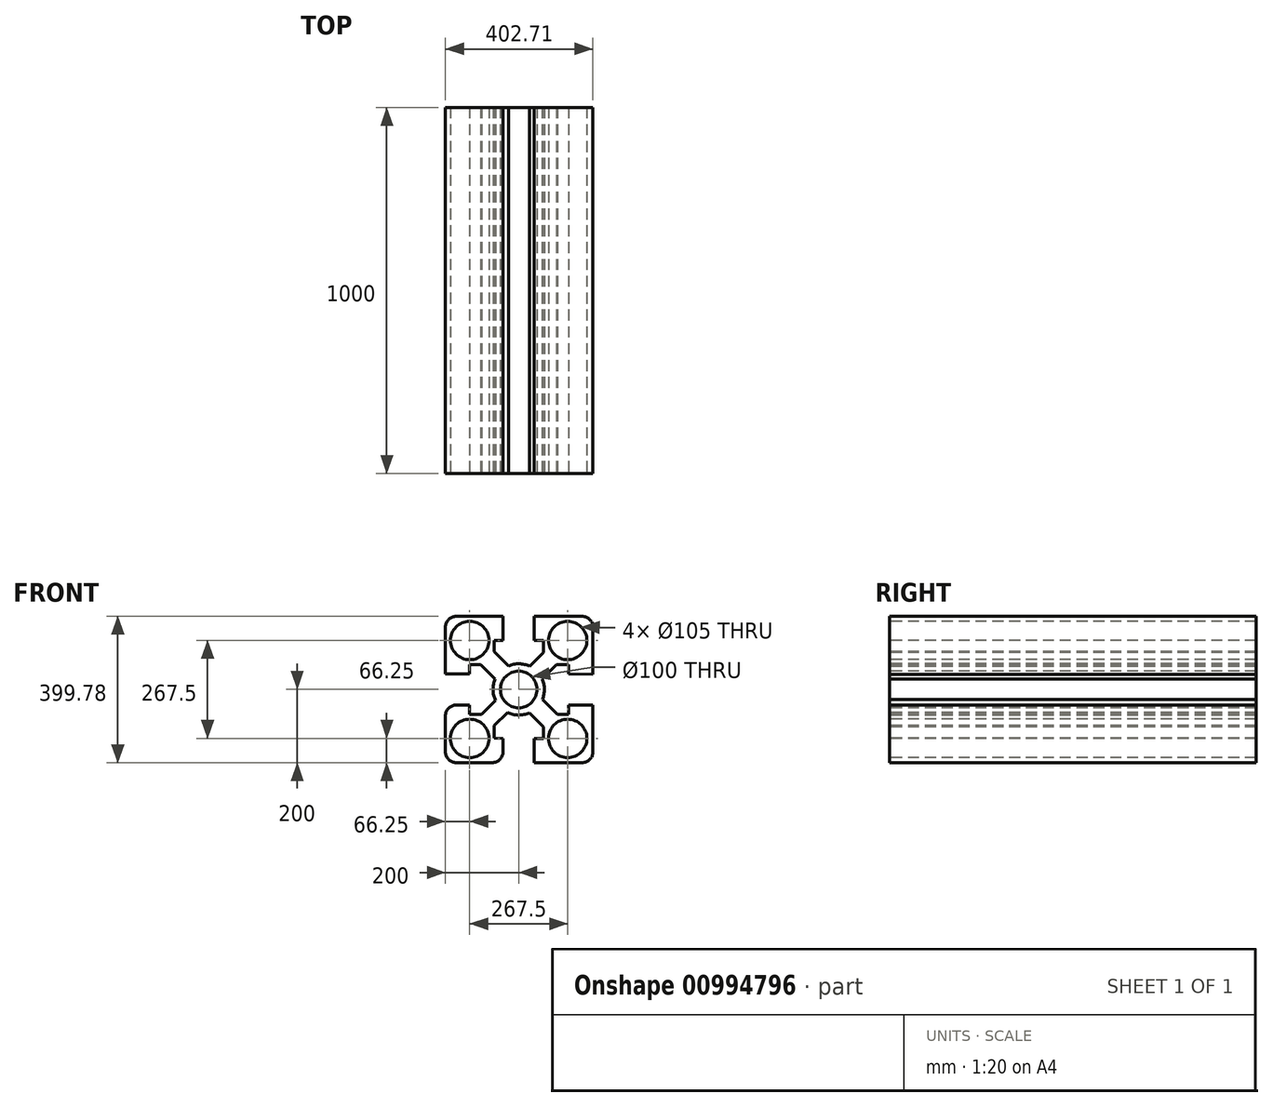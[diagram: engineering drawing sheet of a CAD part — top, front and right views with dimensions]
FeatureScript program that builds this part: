
annotation { "Feature Type Name" : "Feature", "Feature Type Description" : "" }
export const myFeature = defineFeature(function(context is Context, id is Id, definition is map)
    precondition{}
    {
        {
            var Q0;
            Q0=qCreatedBy(makeId("Front.planeOp"),FACE);
            var sketch = newSketch(context, id + "F0", { "sketchPlane" : qUnion([Q0])});
            skLineSegment(sketch, "E0", {"start": v(-200, -200) * mm, "end": v(-200, -133.75) * mm});
            skLineSegment(sketch, "E1", {"start": v(202.71, 199.78) * mm, "end": v(42.5, 199.78) * mm});
            skLineSegment(sketch, "E2", {"start": v(42.5, 199.78) * mm, "end": v(42.5, 133.75) * mm});
            skLineSegment(sketch, "E3", {"start": v(42.5, 133.75) * mm, "end": v(67.5, 133.75) * mm});
            skLineSegment(sketch, "E4", {"start": v(67.5, 133.75) * mm, "end": v(67.5, 100.95) * mm});
            skLineSegment(sketch, "E5", {"start": v(-100.85, -67.6) * mm, "end": v(-133.75, -67.6) * mm});
            skLineSegment(sketch, "E6", {"start": v(-133.75, -67.6) * mm, "end": v(-133.75, -42.5) * mm});
            skLineSegment(sketch, "E7", {"start": v(-133.75, -42.5) * mm, "end": v(-200, -42.5) * mm});
            skLineSegment(sketch, "E8", {"start": v(-200, -42.5) * mm, "end": v(-200, -200) * mm});
            skLineSegment(sketch, "E9", {"start": v(-42.5, -200) * mm, "end": v(-42.5, -133.75) * mm});
            skLineSegment(sketch, "E10", {"start": v(-42.5, -133.75) * mm, "end": v(-67.5, -133.3) * mm});
            skLineSegment(sketch, "E11", {"start": v(-67.5, -133.3) * mm, "end": v(-67.5, -98.5) * mm});
            skLineSegment(sketch, "E12", {"start": v(103.73, 67.4) * mm, "end": v(136.46, 67.4) * mm});
            skLineSegment(sketch, "E13", {"start": v(136.46, 67.4) * mm, "end": v(136.46, 42.5) * mm});
            skLineSegment(sketch, "E14", {"start": v(136.46, 42.5) * mm, "end": v(202.71, 41.3) * mm});
            skLineSegment(sketch, "E15", {"start": v(202.71, 41.3) * mm, "end": v(202.71, 199.78) * mm});
            skLineSegment(sketch, "E16", {"start": v(-42.5, 133.75) * mm, "end": v(-67.5, 133.75) * mm});
            skLineSegment(sketch, "E17", {"start": v(-67.5, 133.75) * mm, "end": v(-67.5, 103.43) * mm});
            skLineSegment(sketch, "E18", {"start": v(105.64, -67.6) * mm, "end": v(136.46, -67.6) * mm});
            skLineSegment(sketch, "E19", {"start": v(136.46, -67.6) * mm, "end": v(136.46, -42.5) * mm});
            skLineSegment(sketch, "E20", {"start": v(136.46, -42.5) * mm, "end": v(202.71, -42.5) * mm});
            skLineSegment(sketch, "E21", {"start": v(202.71, -42.5) * mm, "end": v(202.71, -200) * mm});
            skLineSegment(sketch, "E22", {"start": v(42.5, -200) * mm, "end": v(42.5, -133.75) * mm});
            skLineSegment(sketch, "E23", {"start": v(42.5, -133.75) * mm, "end": v(67.5, -133.75) * mm});
            skLineSegment(sketch, "E24", {"start": v(67.5, -133.75) * mm, "end": v(67.5, -102.08) * mm});
            skLineSegment(sketch, "E25", {"start": v(-103.34, 67.4) * mm, "end": v(-133.75, 67.4) * mm});
            skLineSegment(sketch, "E26", {"start": v(-133.75, 67.4) * mm, "end": v(-133.75, 42.5) * mm});
            skLineSegment(sketch, "E27", {"start": v(-133.75, 42.5) * mm, "end": v(-200, 42.5) * mm});
            skLineSegment(sketch, "E28", {"start": v(-200, 42.5) * mm, "end": v(-200, 199.78) * mm});
            skLineSegment(sketch, "E29", {"start": v(-42.5, -200) * mm, "end": v(-200, -200) * mm});
            skLineSegment(sketch, "E30", {"start": v(42.5, -200) * mm, "end": v(202.71, -200) * mm});
            skLineSegment(sketch, "E31", {"start": v(-42.5, 133.75) * mm, "end": v(-42.5, 199.78) * mm});
            skLineSegment(sketch, "E32", {"start": v(-200, 199.78) * mm, "end": v(-42.5, 199.78) * mm});
            skCircle(sketch, "E33", {"center": v(0, 0) * mm, "radius": 70 * mm});
            skLineSegment(sketch, "E34", {"start": v(-67.5, 103.43) * mm, "end": v(-27.82, 64.23) * mm});
            skLineSegment(sketch, "E35", {"start": v(-103.34, 67.4) * mm, "end": v(-64, 28.37) * mm});
            skLineSegment(sketch, "E36", {"start": v(64.57, -27.03) * mm, "end": v(105.64, -67.6) * mm});
            skLineSegment(sketch, "E37", {"start": v(28.88, -63.77) * mm, "end": v(67.5, -102.08) * mm});
            skLineSegment(sketch, "E38", {"start": v(29.9, 63.3) * mm, "end": v(67.5, 100.95) * mm});
            skLineSegment(sketch, "E39", {"start": v(63.83, 28.74) * mm, "end": v(103.73, 67.4) * mm});
            skLineSegment(sketch, "E40", {"start": v(-30.75, -62.89) * mm, "end": v(-67.5, -98.5) * mm});
            skLineSegment(sketch, "E41", {"start": v(-63.26, -29.97) * mm, "end": v(-100.85, -67.6) * mm});
            skSolve(sketch);
        }
        {
            var Q0;
            Q0 = qSketchRegion(id + "F0", true);
            extrude(context, id + "F1", {"entities" : qUnion([Q0]), "oppositeDirection" : true, "depth" : 1000 * mm, "offsetDistance" : 25.4 * mm});
        }
        {
            var Q0;
            Q0=makeQuery(id+"F0.imprint","IMPRINT",FACE,{"disambiguationData":[TD([[makeQuery(id+"F0.imprint","IMPRINT",EDGE,{"derivedFrom":sQuery(id+"F0.wireOp",EDGE,"E1")}),1.0]])]});
            var sketch = newSketch(context, id + "F2", { "sketchPlane" : qUnion([Q0])});
            skCircle(sketch, "E42", {"center": v(0, 0) * mm, "radius": 50 * mm});
            skCircle(sketch, "E43", {"center": v(-133.75, 133.75) * mm, "radius": 52.5 * mm});
            skCircle(sketch, "E44.1.0", {"center": v(133.75, 133.75) * mm, "radius": 52.5 * mm});
            skCircle(sketch, "E44.2.0", {"center": v(133.75, -133.75) * mm, "radius": 52.5 * mm});
            skCircle(sketch, "E44.3.0", {"center": v(-133.75, -133.75) * mm, "radius": 52.5 * mm});
            skLineSegment(sketch, "E44.anchor1", {"start": v(0, 0) * mm, "end": v(-133.75, 133.75) * mm, "construction": true});
            skLineSegment(sketch, "E44.anchor2", {"start": v(0, 0) * mm, "end": v(-133.75, -133.75) * mm, "construction": true});
            skSolve(sketch);
        }
        {
            var Q0;
            Q0 = qSketchRegion(id + "F2", true);
            extrude(context, id + "F3", {"entities" : qUnion([Q0]), "operationType" : NewBodyOperationType.REMOVE, "oppositeDirection" : true, "depth" : 2000 * mm, "offsetDistance" : 25.4 * mm});
        }
        {
            var Q0;
            Q0=makeQuery(id+"F1.opExtrude","SWEPT_EDGE",EDGE,{"disambiguationData":[OSD([sQuery(id+"F0.wireOp",EDGE,"E1"),sQuery(id+"F0.wireOp",EDGE,"E15")])]});
            var Q1;
            Q1=makeQuery(id+"F1.opExtrude","SWEPT_EDGE",EDGE,{"disambiguationData":[OSD([sQuery(id+"F0.wireOp",EDGE,"E28"),sQuery(id+"F0.wireOp",EDGE,"E32")])]});
            var Q2;
            Q2=makeQuery(id+"F1.opExtrude","SWEPT_EDGE",EDGE,{"disambiguationData":[OSD([sQuery(id+"F0.wireOp",EDGE,"E21"),sQuery(id+"F0.wireOp",EDGE,"E30")])]});
            var Q3;
            Q3=makeQuery(id+"F1.opExtrude","SWEPT_EDGE",EDGE,{"disambiguationData":[OSD([sQuery(id+"F0.wireOp",EDGE,"E8"),sQuery(id+"F0.wireOp",EDGE,"E29")])]});
            fillet(context, id + "F4", {"entities" : qUnion([Q0, Q1, Q2, Q3]), "radius" : 30 * mm, "tangentPropagation" : true, "allowEdgeOverflow" : false});
        }
    });
